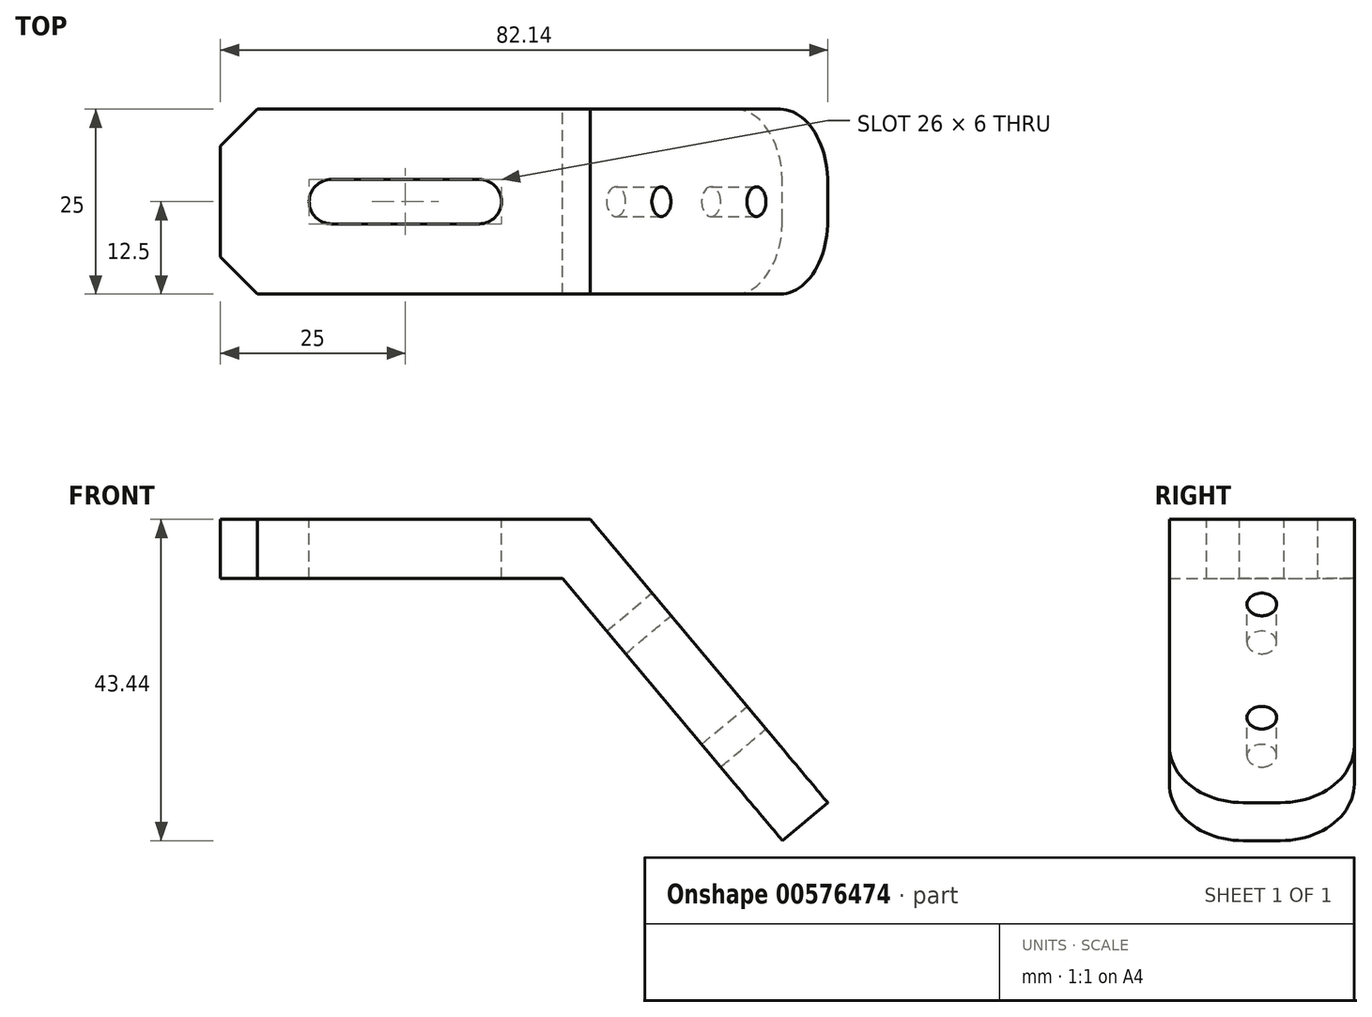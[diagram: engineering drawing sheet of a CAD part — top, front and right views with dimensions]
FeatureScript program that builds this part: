
annotation { "Feature Type Name" : "Feature", "Feature Type Description" : "" }
export const myFeature = defineFeature(function(context is Context, id is Id, definition is map)
    precondition{}
    {
        {
            var Q0;
            Q0=qCreatedBy(makeId("Front.planeOp"),FACE);
            var sketch = newSketch(context, id + "F0", { "sketchPlane" : qUnion([Q0])});
            skLineSegment(sketch, "E0", {"start": v(0, 0) * mm, "end": v(46.27, 0) * mm});
            skLineSegment(sketch, "E1", {"start": v(46.27, 0) * mm, "end": v(76.01, -35.44) * mm});
            skLineSegment(sketch, "E2.0", {"start": v(50, 8) * mm, "end": v(82.14, -30.3) * mm});
            skLineSegment(sketch, "E2.1", {"start": v(0, 8) * mm, "end": v(50, 8) * mm});
            skLineSegment(sketch, "E3", {"start": v(0, 8) * mm, "end": v(0, 0) * mm});
            skLineSegment(sketch, "E4", {"start": v(76.01, -35.44) * mm, "end": v(82.14, -30.3) * mm});
            skSolve(sketch);
        }
        {
            var Q0;
            Q0 = qSketchRegion(id + "F0", true);
            extrude(context, id + "F1", {"entities" : qUnion([Q0]), "endBound" : BoundingType.SYMMETRIC, "depth" : 25 * mm, "offsetDistance" : 25 * mm});
        }
        {
            var Q0;
            Q0=makeQuery(id+"F1.opExtrude","SWEPT_FACE",FACE,{"disambiguationData":[OSD([sQuery(id+"F0.wireOp",EDGE,"E2.1")])]});
            var sketch = newSketch(context, id + "F2", { "sketchPlane" : qUnion([Q0])});
            skLineSegment(sketch, "E5", {"start": v(15, 0) * mm, "end": v(35, 0) * mm});
            skArc(sketch, "E6.0.startCap", {"start": v(15, -3) * mm, "mid": v(12, 0) * mm, "end": v(15, 3) * mm});
            skArc(sketch, "E6.0.endCap", {"start": v(35, 3) * mm, "mid": v(38, 0) * mm, "end": v(35, -3) * mm});
            skLineSegment(sketch, "E6.0.left", {"start": v(15, 3) * mm, "end": v(35, 3) * mm});
            skLineSegment(sketch, "E6.0.right", {"start": v(15, -3) * mm, "end": v(35, -3) * mm});
            skSolve(sketch);
        }
        {
            var Q0;
            Q0 = qSketchRegion(id + "F2", true);
            extrude(context, id + "F3", {"entities" : qUnion([Q0]), "operationType" : NewBodyOperationType.REMOVE, "endBound" : BoundingType.THROUGH_ALL, "oppositeDirection" : true, "depth" : 25 * mm, "offsetDistance" : 25 * mm});
        }
        {
            var Q0;
            Q0=makeQuery(id+"F1.opExtrude","SWEPT_FACE",FACE,{"disambiguationData":[OSD([sQuery(id+"F0.wireOp",EDGE,"E2.0")])]});
            var sketch = newSketch(context, id + "F4", { "sketchPlane" : qUnion([Q0])});
            skPoint(sketch, "E7", {"position": v(0, -41.01) * mm});
            skPoint(sketch, "E7.positionSnap0", {"position": v(0, -26.01) * mm});
            skPoint(sketch, "E8", {"position": v(0, -61.01) * mm});
            skSolve(sketch);
        }
        {
            var Q0;
            Q0=sQuery(id+"F4.wireOp",VERTEX,"E7");
            var Q1;
            Q1=sQuery(id+"F4.wireOp",VERTEX,"E8");
            var Q2;
            Q2=makeQuery(id+"F1.opExtrude","SWEPT_BODY",BODY,{"disambiguationData":[OSD([sQuery(id+"F0.wireOp",EDGE,"E0"),sQuery(id+"F0.wireOp",EDGE,"E1"),sQuery(id+"F0.wireOp",EDGE,"E2.0"),sQuery(id+"F0.wireOp",EDGE,"E2.1"),sQuery(id+"F0.wireOp",EDGE,"E3"),sQuery(id+"F0.wireOp",EDGE,"E4")])]});
            hole(context, id + "F5", {"style" : HoleStyle.SIMPLE, "endStyle" : HoleEndStyle.THROUGH, "holeDiameter" : 4 * mm, "isTappedThrough" : true, "tappedDepth" : 12 * mm, "tapClearance" : 3, "locations" : qUnion([Q0, Q1]), "scope" : qUnion([Q2])});
        }
        {
            var Q0;
            Q0=makeQuery(id+"F1.opExtrude","CAP_EDGE",EDGE,{"disambiguationData":[OSD([sQuery(id+"F0.wireOp",EDGE,"E4")])],"isStart":false});
            var Q1;
            Q1=makeQuery(id+"F1.opExtrude","CAP_EDGE",EDGE,{"disambiguationData":[OSD([sQuery(id+"F0.wireOp",EDGE,"E4")])],"isStart":true});
            fillet(context, id + "F6", {"entities" : qUnion([Q0, Q1]), "radius" : 10 * mm, "tangentPropagation" : true, "allowEdgeOverflow" : false});
        }
        {
            var Q0;
            Q0=makeQuery(id+"F1.opExtrude","CAP_EDGE",EDGE,{"disambiguationData":[OSD([sQuery(id+"F0.wireOp",EDGE,"E3")])],"isStart":false});
            var Q1;
            Q1=makeQuery(id+"F1.opExtrude","CAP_EDGE",EDGE,{"disambiguationData":[OSD([sQuery(id+"F0.wireOp",EDGE,"E3")])],"isStart":true});
            chamfer(context, id + "F7", {"entities" : qUnion([Q0, Q1]), "width" : 5 * mm, "tangentPropagation" : true});
        }
    });
